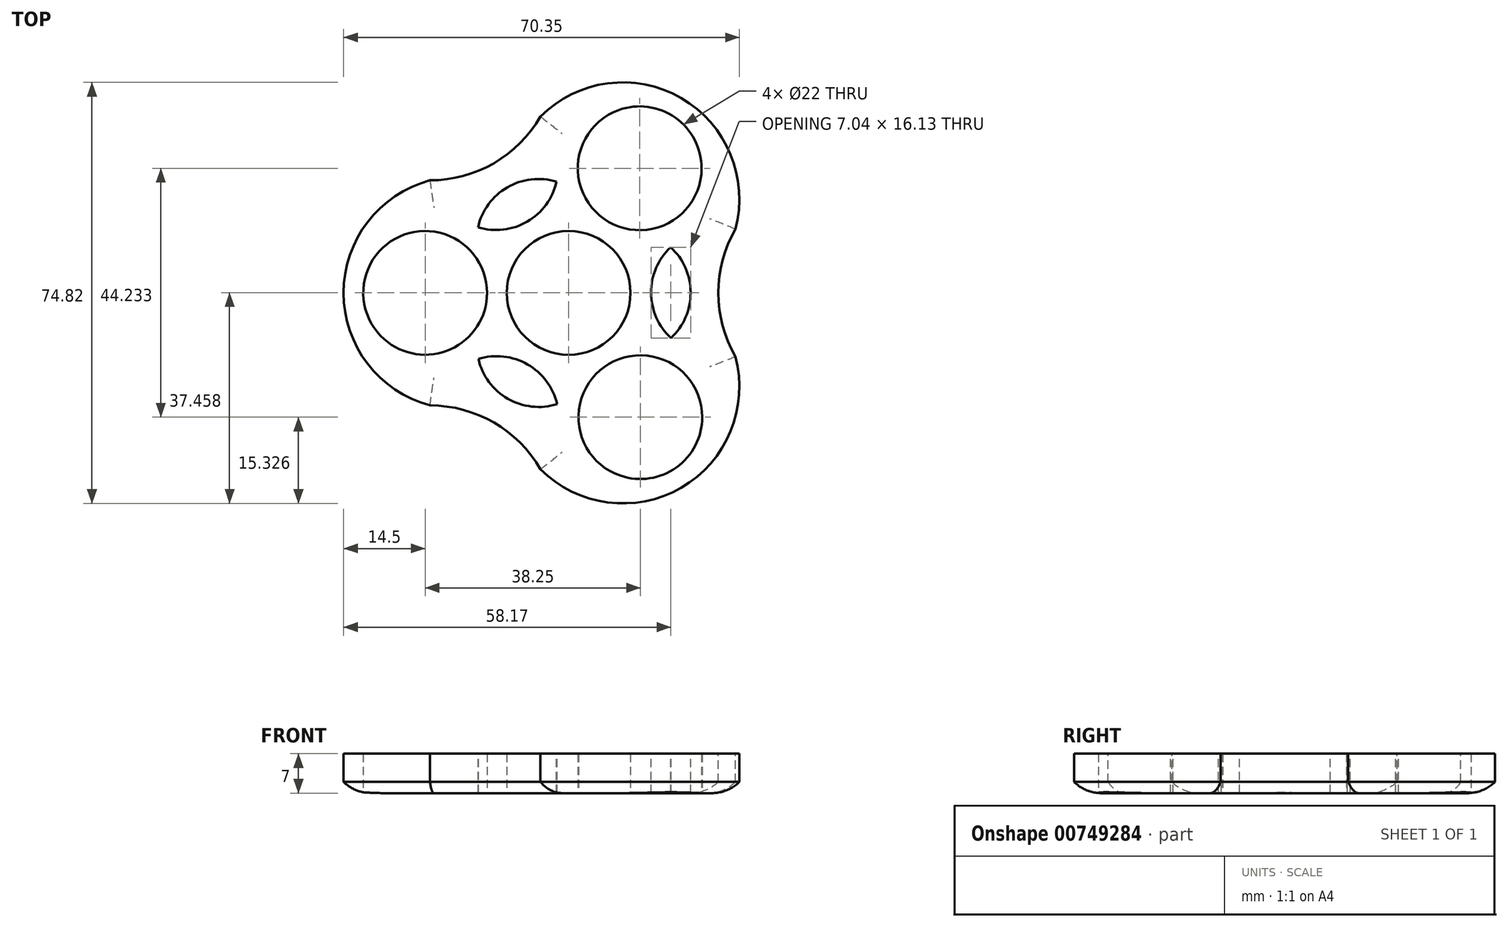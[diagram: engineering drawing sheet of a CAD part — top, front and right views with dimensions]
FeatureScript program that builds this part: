
annotation { "Feature Type Name" : "Feature", "Feature Type Description" : "" }
export const myFeature = defineFeature(function(context is Context, id is Id, definition is map)
    precondition{}
    {
        {
            var Q0;
            Q0=qCreatedBy(makeId("Top.planeOp"),FACE);
            var sketch = newSketch(context, id + "F0", { "sketchPlane" : qUnion([Q0])});
            skCircle(sketch, "E0", {"center": v(0, 0) * mm, "radius": 40 * mm});
            skCircle(sketch, "E1", {"center": v(0, 0) * mm, "radius": 11 * mm});
            skLineSegment(sketch, "E2", {"start": v(-11, 0) * mm, "end": v(-14.5, 0) * mm});
            skLineSegment(sketch, "E3", {"start": v(-14.5, 0) * mm, "end": v(-25.5, 0) * mm});
            skCircle(sketch, "E4", {"center": v(-25.5, 0) * mm, "radius": 11 * mm});
            skLineSegment(sketch, "E5", {"start": v(0, 0) * mm, "end": v(0, -40) * mm});
            skLineSegment(sketch, "E6", {"start": v(0, 0) * mm, "end": v(7.25, -12.56) * mm});
            skLineSegment(sketch, "E7", {"start": v(7.25, -12.56) * mm, "end": v(12.75, -22.08) * mm});
            skCircle(sketch, "E8", {"center": v(12.75, -22.08) * mm, "radius": 11 * mm});
            skLineSegment(sketch, "E9", {"start": v(0, 0) * mm, "end": v(0, 40) * mm});
            skLineSegment(sketch, "E10", {"start": v(0, 0) * mm, "end": v(7.25, 12.56) * mm});
            skLineSegment(sketch, "E11", {"start": v(7.25, 12.56) * mm, "end": v(12.63, 22.15) * mm});
            skCircle(sketch, "E12", {"center": v(12.63, 22.15) * mm, "radius": 11 * mm});
            skSolve(sketch);
        }
        {
            var Q0;
            Q0=makeQuery(id+"F0.imprint","IMPRINT",FACE,{"disambiguationData":[TD([[makeQuery(id+"F0.imprint","IMPRINT",EDGE,{"derivedFrom":sQuery(id+"F0.wireOp",EDGE,"E4")}),-1.0]])]});
            var Q1;
            Q1=makeQuery(id+"F0.imprint","IMPRINT",FACE,{"disambiguationData":[TD([[makeQuery(id+"F0.imprint","IMPRINT",EDGE,{"derivedFrom":sQuery(id+"F0.wireOp",EDGE,"E8")}),-1.0]])]});
            extrude(context, id + "F1", {"entities" : qUnion([Q0, Q1]), "depth" : 7 * mm, "offsetDistance" : 25 * mm});
        }
        {
            var Q0;
            Q0=makeQuery(id+"F1.opExtrude","CAP_FACE",FACE,{"disambiguationData":[OSD([sQuery(id+"F0.wireOp",EDGE,"E0"),sQuery(id+"F0.wireOp",EDGE,"E1"),sQuery(id+"F0.wireOp",EDGE,"E4"),sQuery(id+"F0.wireOp",EDGE,"E8"),sQuery(id+"F0.wireOp",EDGE,"E12")])],"isStart":false});
            var sketch = newSketch(context, id + "F2", { "sketchPlane" : qUnion([Q0])});
            skLineSegment(sketch, "E13", {"start": v(0, 0) * mm, "end": v(-40, 0) * mm});
            skLineSegment(sketch, "E14", {"start": v(0, 0) * mm, "end": v(25.32, -43.86) * mm});
            skLineSegment(sketch, "E15", {"start": v(0, 0) * mm, "end": v(28.72, 49.74) * mm});
            skLineSegment(sketch, "E16", {"start": v(-40, 0) * mm, "end": v(-40, 20) * mm});
            skLineSegment(sketch, "E17", {"start": v(-40, 0) * mm, "end": v(-40, -20) * mm});
            skLineSegment(sketch, "E18", {"start": v(-40, 20) * mm, "end": v(-34.64, 20) * mm});
            skLineSegment(sketch, "E19", {"start": v(-40, -20) * mm, "end": v(-34.64, -20) * mm});
            skLineSegment(sketch, "E20", {"start": v(25.32, -43.86) * mm, "end": v(20, -34.64) * mm});
            skLineSegment(sketch, "E21", {"start": v(20, -34.64) * mm, "end": v(2.68, -44.64) * mm});
            skLineSegment(sketch, "E22", {"start": v(20, -34.64) * mm, "end": v(37.32, -24.64) * mm});
            skLineSegment(sketch, "E23", {"start": v(28.72, 49.74) * mm, "end": v(20, 34.64) * mm});
            skLineSegment(sketch, "E24", {"start": v(20, 34.64) * mm, "end": v(37.32, 24.64) * mm});
            skLineSegment(sketch, "E25", {"start": v(20, 34.64) * mm, "end": v(2.68, 44.64) * mm});
            skLineSegment(sketch, "E26", {"start": v(2.68, 44.64) * mm, "end": v(0, 40) * mm});
            skLineSegment(sketch, "E27", {"start": v(37.32, 24.64) * mm, "end": v(34.64, 20) * mm});
            skLineSegment(sketch, "E28", {"start": v(2.68, -44.64) * mm, "end": v(0, -40) * mm});
            skLineSegment(sketch, "E29", {"start": v(37.32, -24.64) * mm, "end": v(34.64, -20) * mm});
            skLineSegment(sketch, "E30", {"start": v(34.64, 20) * mm, "end": v(29.64, 11.34) * mm});
            skArc(sketch, "E31", {"start": v(29.64, 11.34) * mm, "mid": v(28.78, 24.63) * mm, "end": v(20, 34.64) * mm});
            skLineSegment(sketch, "E32", {"start": v(34.64, -20) * mm, "end": v(29.64, -11.34) * mm});
            skArc(sketch, "E33", {"start": v(20, -34.64) * mm, "mid": v(28.78, -24.63) * mm, "end": v(29.64, -11.34) * mm});
            skArc(sketch, "E34", {"start": v(29.64, 11.34) * mm, "mid": v(26.6, 0) * mm, "end": v(29.64, -11.34) * mm});
            skLineSegment(sketch, "E35", {"start": v(0, 40) * mm, "end": v(-5, 31.34) * mm});
            skLineSegment(sketch, "E36", {"start": v(-34.64, 20) * mm, "end": v(-24.64, 20) * mm});
            skArc(sketch, "E37", {"start": v(-24.64, 20) * mm, "mid": v(-35.72, 12.6) * mm, "end": v(-40, 0) * mm});
            skArc(sketch, "E38", {"start": v(20, 34.64) * mm, "mid": v(6.94, 37.24) * mm, "end": v(-5, 31.34) * mm});
            skArc(sketch, "E39", {"start": v(-24.64, 20) * mm, "mid": v(-13.3, 23.04) * mm, "end": v(-5, 31.34) * mm});
            skLineSegment(sketch, "E40", {"start": v(-34.64, -20) * mm, "end": v(-24.64, -20) * mm});
            skLineSegment(sketch, "E41", {"start": v(0, -40) * mm, "end": v(-5, -31.34) * mm});
            skArc(sketch, "E42", {"start": v(-40, 0) * mm, "mid": v(-35.72, -12.6) * mm, "end": v(-24.64, -20) * mm});
            skArc(sketch, "E43", {"start": v(-5, -31.34) * mm, "mid": v(6.94, -37.24) * mm, "end": v(20, -34.64) * mm});
            skArc(sketch, "E44", {"start": v(-5, -31.34) * mm, "mid": v(-13.3, -23.04) * mm, "end": v(-24.64, -20) * mm});
            skSolve(sketch);
        }
        {
            var Q0;
            {var subQ0=sQuery(id+"F2.wireOp",EDGE,"E35");Q0=makeQuery(id+"F2.imprint","IMPRINT",FACE,{"disambiguationData":[TD([[makeQuery(id+"F2.imprint","IMPRINT",EDGE,{"derivedFrom":subQ0}),-1.0]])]});}
            var Q1;
            {var subQ0=sQuery(id+"F2.wireOp",EDGE,"E35");Q1=makeQuery(id+"F2.imprint","IMPRINT",FACE,{"disambiguationData":[TD([[makeQuery(id+"F2.imprint","IMPRINT",EDGE,{"derivedFrom":subQ0}),1.0]])]});}
            var Q2;
            {var subQ0=sQuery(id+"F2.wireOp",EDGE,"E36");Q2=makeQuery(id+"F2.imprint","IMPRINT",FACE,{"disambiguationData":[TD([[makeQuery(id+"F2.imprint","IMPRINT",EDGE,{"derivedFrom":subQ0}),-1.0]])]});}
            var Q3;
            {var subQ0=sQuery(id+"F2.wireOp",EDGE,"E40");Q3=makeQuery(id+"F2.imprint","IMPRINT",FACE,{"disambiguationData":[TD([[makeQuery(id+"F2.imprint","IMPRINT",EDGE,{"derivedFrom":subQ0}),1.0]])]});}
            var Q4;
            {var subQ0=sQuery(id+"F2.wireOp",EDGE,"E40");Q4=makeQuery(id+"F2.imprint","IMPRINT",FACE,{"disambiguationData":[TD([[makeQuery(id+"F2.imprint","IMPRINT",EDGE,{"derivedFrom":subQ0}),-1.0]])]});}
            var Q5;
            {var subQ0=sQuery(id+"F2.wireOp",EDGE,"E41");Q5=makeQuery(id+"F2.imprint","IMPRINT",FACE,{"disambiguationData":[TD([[makeQuery(id+"F2.imprint","IMPRINT",EDGE,{"derivedFrom":subQ0}),-1.0]])]});}
            var Q6;
            {var subQ0=sQuery(id+"F2.wireOp",EDGE,"E32");Q6=makeQuery(id+"F2.imprint","IMPRINT",FACE,{"disambiguationData":[TD([[makeQuery(id+"F2.imprint","IMPRINT",EDGE,{"derivedFrom":subQ0}),1.0]])]});}
            var Q7;
            {var subQ0=sQuery(id+"F2.wireOp",EDGE,"E30");Q7=makeQuery(id+"F2.imprint","IMPRINT",FACE,{"disambiguationData":[TD([[makeQuery(id+"F2.imprint","IMPRINT",EDGE,{"derivedFrom":subQ0}),1.0]])]});}
            var Q8;
            {var subQ0=sQuery(id+"F2.wireOp",EDGE,"E30");Q8=makeQuery(id+"F2.imprint","IMPRINT",FACE,{"disambiguationData":[TD([[makeQuery(id+"F2.imprint","IMPRINT",EDGE,{"derivedFrom":subQ0}),-1.0]])]});}
            extrude(context, id + "F3", {"entities" : qUnion([Q0, Q1, Q2, Q3, Q4, Q5, Q6, Q7, Q8]), "operationType" : NewBodyOperationType.REMOVE, "oppositeDirection" : true, "depth" : 25 * mm, "offsetDistance" : 25 * mm});
        }
        {
            var Q0;
            Q0=makeQuery(id+"F1.opExtrude","CAP_FACE",FACE,{"disambiguationData":[OSD([sQuery(id+"F0.wireOp",EDGE,"E0"),sQuery(id+"F0.wireOp",EDGE,"E1"),sQuery(id+"F0.wireOp",EDGE,"E4"),sQuery(id+"F0.wireOp",EDGE,"E8"),sQuery(id+"F0.wireOp",EDGE,"E12")])],"isStart":false});
            var sketch = newSketch(context, id + "F4", { "sketchPlane" : qUnion([Q0])});
            skArc(sketch, "E45", {"start": v(12.63, 22.15) * mm, "mid": v(-9.4, 16.2) * mm, "end": v(-25.5, 0) * mm});
            skLineSegment(sketch, "E46", {"start": v(-18.89, 8.8) * mm, "end": v(-16.1, 11.66) * mm});
            skLineSegment(sketch, "E47", {"start": v(1.72, 20.76) * mm, "end": v(-2.15, 19.76) * mm});
            skArc(sketch, "E48", {"start": v(-2.15, 19.76) * mm, "mid": v(-10.9, 18.76) * mm, "end": v(-16.1, 11.66) * mm});
            skArc(sketch, "E49", {"start": v(-16.1, 11.66) * mm, "mid": v(-7.36, 12.67) * mm, "end": v(-2.15, 19.76) * mm});
            skSolve(sketch);
        }
        {
            var Q0;
            {var subQ4=sQuery(id+"F4.wireOp",EDGE,"E48");Q0=makeQuery(id+"F4.imprint","IMPRINT",FACE,{"disambiguationData":[TD([[makeQuery(id+"F4.imprint","IMPRINT",EDGE,{"derivedFrom":subQ4}),1.0]])]});}
            var Q1;
            {var subQ0=sQuery(id+"F4.wireOp",EDGE,"E49");var subQ1=sQuery(id+"F4.wireOp",EDGE,"E45");var subQ2=makeQuery(id+"F4.imprint","INTERSECT",VERTEX,{"disambiguationData":[OD(0.0)],"derivedFrom":[subQ1,subQ0]});Q1=makeQuery(id+"F4.imprint","IMPRINT",FACE,{"disambiguationData":[TD([[makeQuery(id+"F4.imprint","IMPRINT",EDGE,{"disambiguationData":[TD([[subQ2,-1.0]])],"derivedFrom":subQ1}),1.0]])]});}
            extrude(context, id + "F5", {"entities" : qUnion([Q0, Q1]), "operationType" : NewBodyOperationType.REMOVE, "oppositeDirection" : true, "depth" : 25 * mm, "offsetDistance" : 25 * mm});
        }
        {
            var Q0;
            {var subQ4=sQuery(id+"F4.wireOp",EDGE,"E48");Q0=makeQuery(id+"F4.imprint","IMPRINT",FACE,{"disambiguationData":[TD([[makeQuery(id+"F4.imprint","IMPRINT",EDGE,{"derivedFrom":subQ4}),1.0]])]});}
            var Q1;
            {var subQ0=sQuery(id+"F4.wireOp",EDGE,"E49");var subQ1=sQuery(id+"F4.wireOp",EDGE,"E45");var subQ2=makeQuery(id+"F4.imprint","INTERSECT",VERTEX,{"disambiguationData":[OD(0.0)],"derivedFrom":[subQ1,subQ0]});Q1=makeQuery(id+"F4.imprint","IMPRINT",FACE,{"disambiguationData":[TD([[makeQuery(id+"F4.imprint","IMPRINT",EDGE,{"disambiguationData":[TD([[subQ2,-1.0]])],"derivedFrom":subQ1}),1.0]])]});}
            extrude(context, id + "F6", {"entities" : qUnion([Q0, Q1]), "operationType" : NewBodyOperationType.ADD, "depth" : 25 * mm, "offsetDistance" : 25 * mm});
        }
        {
            var Q0;
            Q0=makeQuery(id+"F6.opExtrude","SWEPT_BODY",BODY,{"disambiguationData":[OSD([sQuery(id+"F4.wireOp",EDGE,"E48"),sQuery(id+"F4.wireOp",EDGE,"E49")])]});
            var Q1;
            Q1=makeQuery(id+"F1.opExtrude","CAP_EDGE",EDGE,{"disambiguationData":[OSD([sQuery(id+"F0.wireOp",EDGE,"E1")])],"isStart":false});
            circularPattern(context, id + "F7", {"entities" : qUnion([Q0]), "axis" : qUnion([Q1]), "angle" : 360 * degree, "instanceCount" : 3, "equalSpace" : true});
        }
        {
            var Q0;
            Q0=makeQuery(id+"F7.opPattern","COPY",FACE,{"derivedFrom":makeQuery(id+"F6.opExtrude","CAP_FACE",FACE,{"disambiguationData":[OSD([sQuery(id+"F4.wireOp",EDGE,"E48"),sQuery(id+"F4.wireOp",EDGE,"E49")])],"isStart":false}),"instanceName":"2"});
            extrude(context, id + "F8", {"entities" : qUnion([Q0]), "operationType" : NewBodyOperationType.REMOVE, "endBound" : BoundingType.THROUGH_ALL, "oppositeDirection" : true, "depth" : 1000 * mm, "offsetDistance" : 25 * mm});
        }
        {
            var Q0;
            Q0=makeQuery(id+"F7.opPattern","COPY",FACE,{"derivedFrom":makeQuery(id+"F6.opExtrude","CAP_FACE",FACE,{"disambiguationData":[OSD([sQuery(id+"F4.wireOp",EDGE,"E48"),sQuery(id+"F4.wireOp",EDGE,"E49")])],"isStart":false}),"instanceName":"1"});
            var Q1;
            Q1=makeQuery(id+"F6.opExtrude","CAP_FACE",FACE,{"disambiguationData":[OSD([sQuery(id+"F4.wireOp",EDGE,"E48"),sQuery(id+"F4.wireOp",EDGE,"E49")])],"isStart":false});
            extrude(context, id + "F9", {"entities" : qUnion([Q0, Q1]), "operationType" : NewBodyOperationType.REMOVE, "endBound" : BoundingType.THROUGH_ALL, "oppositeDirection" : true, "depth" : 25 * mm, "offsetDistance" : 25 * mm});
        }
        {
            var Q0;
            Q0=makeQuery(id+"F3.boolean.opBoolean","COPY",EDGE,{"derivedFrom":makeQuery(id+"F3.opExtrude","CAP_EDGE",EDGE,{"disambiguationData":[OSD([sQuery(id+"F2.wireOp",EDGE,"E39")])],"isStart":true})});
            var Q1;
            Q1=makeQuery(id+"F3.boolean.opBoolean","TWEAK_EDGE",EDGE,{"derivedFrom":[makeQuery(id+"F3.opExtrude","CAP_EDGE",EDGE,{"disambiguationData":[OSD([sQuery(id+"F2.wireOp",EDGE,"E37")])],"isStart":true}),makeQuery(id+"F3.opExtrude","CAP_EDGE",EDGE,{"disambiguationData":[OSD([sQuery(id+"F2.wireOp",EDGE,"E42")])],"isStart":true})]});
            var Q2;
            Q2=makeQuery(id+"F3.boolean.opBoolean","TWEAK_EDGE",EDGE,{"derivedFrom":[makeQuery(id+"F3.opExtrude","CAP_EDGE",EDGE,{"disambiguationData":[OSD([sQuery(id+"F2.wireOp",EDGE,"E31")])],"isStart":true}),makeQuery(id+"F3.opExtrude","CAP_EDGE",EDGE,{"disambiguationData":[OSD([sQuery(id+"F2.wireOp",EDGE,"E38")])],"isStart":true})]});
            var Q3;
            Q3=makeQuery(id+"F3.boolean.opBoolean","COPY",EDGE,{"derivedFrom":makeQuery(id+"F3.opExtrude","CAP_EDGE",EDGE,{"disambiguationData":[OSD([sQuery(id+"F2.wireOp",EDGE,"E34")])],"isStart":true})});
            var Q4;
            Q4=makeQuery(id+"F3.boolean.opBoolean","TWEAK_EDGE",EDGE,{"derivedFrom":[makeQuery(id+"F3.opExtrude","CAP_EDGE",EDGE,{"disambiguationData":[OSD([sQuery(id+"F2.wireOp",EDGE,"E33")])],"isStart":true}),makeQuery(id+"F3.opExtrude","CAP_EDGE",EDGE,{"disambiguationData":[OSD([sQuery(id+"F2.wireOp",EDGE,"E43")])],"isStart":true})]});
            var Q5;
            Q5=makeQuery(id+"F3.boolean.opBoolean","COPY",EDGE,{"derivedFrom":makeQuery(id+"F3.opExtrude","CAP_EDGE",EDGE,{"disambiguationData":[OSD([sQuery(id+"F2.wireOp",EDGE,"E44")])],"isStart":true})});
            var Q6;
            Q6=makeQuery(id+"F3.boolean.opBoolean","INTERSECT",EDGE,{"derivedFrom":[makeQuery(id+"F1.opExtrude","CAP_FACE",FACE,{"disambiguationData":[OSD([sQuery(id+"F0.wireOp",EDGE,"E0"),sQuery(id+"F0.wireOp",EDGE,"E1"),sQuery(id+"F0.wireOp",EDGE,"E4"),sQuery(id+"F0.wireOp",EDGE,"E8"),sQuery(id+"F0.wireOp",EDGE,"E12")])],"isStart":true}),makeQuery(id+"F3.opExtrude","SWEPT_FACE",FACE,{"disambiguationData":[OSD([sQuery(id+"F2.wireOp",EDGE,"E37")])]}),makeQuery(id+"F3.opExtrude","SWEPT_FACE",FACE,{"disambiguationData":[OSD([sQuery(id+"F2.wireOp",EDGE,"E42")])]})]});
            var Q7;
            Q7=makeQuery(id+"F3.boolean.opBoolean","INTERSECT",EDGE,{"derivedFrom":[makeQuery(id+"F1.opExtrude","CAP_FACE",FACE,{"disambiguationData":[OSD([sQuery(id+"F0.wireOp",EDGE,"E0"),sQuery(id+"F0.wireOp",EDGE,"E1"),sQuery(id+"F0.wireOp",EDGE,"E4"),sQuery(id+"F0.wireOp",EDGE,"E8"),sQuery(id+"F0.wireOp",EDGE,"E12")])],"isStart":true}),makeQuery(id+"F3.opExtrude","SWEPT_FACE",FACE,{"disambiguationData":[OSD([sQuery(id+"F2.wireOp",EDGE,"E39")])]})]});
            var Q8;
            Q8=makeQuery(id+"F3.boolean.opBoolean","INTERSECT",EDGE,{"derivedFrom":[makeQuery(id+"F1.opExtrude","CAP_FACE",FACE,{"disambiguationData":[OSD([sQuery(id+"F0.wireOp",EDGE,"E0"),sQuery(id+"F0.wireOp",EDGE,"E1"),sQuery(id+"F0.wireOp",EDGE,"E4"),sQuery(id+"F0.wireOp",EDGE,"E8"),sQuery(id+"F0.wireOp",EDGE,"E12")])],"isStart":true}),makeQuery(id+"F3.opExtrude","SWEPT_FACE",FACE,{"disambiguationData":[OSD([sQuery(id+"F2.wireOp",EDGE,"E31")])]}),makeQuery(id+"F3.opExtrude","SWEPT_FACE",FACE,{"disambiguationData":[OSD([sQuery(id+"F2.wireOp",EDGE,"E38")])]})]});
            var Q9;
            Q9=makeQuery(id+"F3.boolean.opBoolean","INTERSECT",EDGE,{"derivedFrom":[makeQuery(id+"F1.opExtrude","CAP_FACE",FACE,{"disambiguationData":[OSD([sQuery(id+"F0.wireOp",EDGE,"E0"),sQuery(id+"F0.wireOp",EDGE,"E1"),sQuery(id+"F0.wireOp",EDGE,"E4"),sQuery(id+"F0.wireOp",EDGE,"E8"),sQuery(id+"F0.wireOp",EDGE,"E12")])],"isStart":true}),makeQuery(id+"F3.opExtrude","SWEPT_FACE",FACE,{"disambiguationData":[OSD([sQuery(id+"F2.wireOp",EDGE,"E34")])]})]});
            var Q10;
            Q10=makeQuery(id+"F3.boolean.opBoolean","INTERSECT",EDGE,{"derivedFrom":[makeQuery(id+"F1.opExtrude","CAP_FACE",FACE,{"disambiguationData":[OSD([sQuery(id+"F0.wireOp",EDGE,"E0"),sQuery(id+"F0.wireOp",EDGE,"E1"),sQuery(id+"F0.wireOp",EDGE,"E4"),sQuery(id+"F0.wireOp",EDGE,"E8"),sQuery(id+"F0.wireOp",EDGE,"E12")])],"isStart":true}),makeQuery(id+"F3.opExtrude","SWEPT_FACE",FACE,{"disambiguationData":[OSD([sQuery(id+"F2.wireOp",EDGE,"E33")])]}),makeQuery(id+"F3.opExtrude","SWEPT_FACE",FACE,{"disambiguationData":[OSD([sQuery(id+"F2.wireOp",EDGE,"E43")])]})]});
            var Q11;
            Q11=makeQuery(id+"F3.boolean.opBoolean","INTERSECT",EDGE,{"derivedFrom":[makeQuery(id+"F1.opExtrude","CAP_FACE",FACE,{"disambiguationData":[OSD([sQuery(id+"F0.wireOp",EDGE,"E0"),sQuery(id+"F0.wireOp",EDGE,"E1"),sQuery(id+"F0.wireOp",EDGE,"E4"),sQuery(id+"F0.wireOp",EDGE,"E8"),sQuery(id+"F0.wireOp",EDGE,"E12")])],"isStart":true}),makeQuery(id+"F3.opExtrude","SWEPT_FACE",FACE,{"disambiguationData":[OSD([sQuery(id+"F2.wireOp",EDGE,"E44")])]})]});
            chamfer(context, id + "F10", {"entities" : qUnion([Q0, Q1, Q2, Q3, Q4, Q5, Q6, Q7, Q8, Q9, Q10, Q11]), "width" : 2 * mm, "tangentPropagation" : true});
        }
        {
            var Q0;
            {var subQ0=makeQuery(id+"F1.opExtrude","CAP_FACE",FACE,{"disambiguationData":[OSD([sQuery(id+"F0.wireOp",EDGE,"E0"),sQuery(id+"F0.wireOp",EDGE,"E1"),sQuery(id+"F0.wireOp",EDGE,"E4"),sQuery(id+"F0.wireOp",EDGE,"E8"),sQuery(id+"F0.wireOp",EDGE,"E12")])],"isStart":true});Q0=makeQuery(id+"F10.opChamfer","BLEND_EDGE",EDGE,{"blendedFrom":[makeQuery(id+"F3.boolean.opBoolean","INTERSECT",EDGE,{"derivedFrom":[subQ0,makeQuery(id+"F3.opExtrude","SWEPT_FACE",FACE,{"disambiguationData":[OSD([sQuery(id+"F2.wireOp",EDGE,"E39")])]})]}),subQ0],"blendedInto":[subQ0]});}
            var Q1;
            {var subQ0=makeQuery(id+"F1.opExtrude","CAP_FACE",FACE,{"disambiguationData":[OSD([sQuery(id+"F0.wireOp",EDGE,"E0"),sQuery(id+"F0.wireOp",EDGE,"E1"),sQuery(id+"F0.wireOp",EDGE,"E4"),sQuery(id+"F0.wireOp",EDGE,"E8"),sQuery(id+"F0.wireOp",EDGE,"E12")])],"isStart":true});Q1=makeQuery(id+"F10.opChamfer","BLEND_EDGE",EDGE,{"blendedFrom":[makeQuery(id+"F3.boolean.opBoolean","INTERSECT",EDGE,{"derivedFrom":[subQ0,makeQuery(id+"F3.opExtrude","SWEPT_FACE",FACE,{"disambiguationData":[OSD([sQuery(id+"F2.wireOp",EDGE,"E37")])]}),makeQuery(id+"F3.opExtrude","SWEPT_FACE",FACE,{"disambiguationData":[OSD([sQuery(id+"F2.wireOp",EDGE,"E42")])]})]}),subQ0],"blendedInto":[subQ0]});}
            var Q2;
            {var subQ0=makeQuery(id+"F1.opExtrude","CAP_FACE",FACE,{"disambiguationData":[OSD([sQuery(id+"F0.wireOp",EDGE,"E0"),sQuery(id+"F0.wireOp",EDGE,"E1"),sQuery(id+"F0.wireOp",EDGE,"E4"),sQuery(id+"F0.wireOp",EDGE,"E8"),sQuery(id+"F0.wireOp",EDGE,"E12")])],"isStart":true});Q2=makeQuery(id+"F10.opChamfer","BLEND_EDGE",EDGE,{"blendedFrom":[makeQuery(id+"F3.boolean.opBoolean","INTERSECT",EDGE,{"derivedFrom":[subQ0,makeQuery(id+"F3.opExtrude","SWEPT_FACE",FACE,{"disambiguationData":[OSD([sQuery(id+"F2.wireOp",EDGE,"E44")])]})]}),subQ0],"blendedInto":[subQ0]});}
            var Q3;
            {var subQ0=makeQuery(id+"F1.opExtrude","CAP_FACE",FACE,{"disambiguationData":[OSD([sQuery(id+"F0.wireOp",EDGE,"E0"),sQuery(id+"F0.wireOp",EDGE,"E1"),sQuery(id+"F0.wireOp",EDGE,"E4"),sQuery(id+"F0.wireOp",EDGE,"E8"),sQuery(id+"F0.wireOp",EDGE,"E12")])],"isStart":true});Q3=makeQuery(id+"F10.opChamfer","BLEND_EDGE",EDGE,{"blendedFrom":[makeQuery(id+"F3.boolean.opBoolean","INTERSECT",EDGE,{"derivedFrom":[subQ0,makeQuery(id+"F3.opExtrude","SWEPT_FACE",FACE,{"disambiguationData":[OSD([sQuery(id+"F2.wireOp",EDGE,"E33")])]}),makeQuery(id+"F3.opExtrude","SWEPT_FACE",FACE,{"disambiguationData":[OSD([sQuery(id+"F2.wireOp",EDGE,"E43")])]})]}),subQ0],"blendedInto":[subQ0]});}
            var Q4;
            {var subQ0=makeQuery(id+"F1.opExtrude","CAP_FACE",FACE,{"disambiguationData":[OSD([sQuery(id+"F0.wireOp",EDGE,"E0"),sQuery(id+"F0.wireOp",EDGE,"E1"),sQuery(id+"F0.wireOp",EDGE,"E4"),sQuery(id+"F0.wireOp",EDGE,"E8"),sQuery(id+"F0.wireOp",EDGE,"E12")])],"isStart":true});Q4=makeQuery(id+"F10.opChamfer","BLEND_EDGE",EDGE,{"blendedFrom":[makeQuery(id+"F3.boolean.opBoolean","INTERSECT",EDGE,{"derivedFrom":[subQ0,makeQuery(id+"F3.opExtrude","SWEPT_FACE",FACE,{"disambiguationData":[OSD([sQuery(id+"F2.wireOp",EDGE,"E34")])]})]}),subQ0],"blendedInto":[subQ0]});}
            var Q5;
            {var subQ0=makeQuery(id+"F1.opExtrude","CAP_FACE",FACE,{"disambiguationData":[OSD([sQuery(id+"F0.wireOp",EDGE,"E0"),sQuery(id+"F0.wireOp",EDGE,"E1"),sQuery(id+"F0.wireOp",EDGE,"E4"),sQuery(id+"F0.wireOp",EDGE,"E8"),sQuery(id+"F0.wireOp",EDGE,"E12")])],"isStart":true});Q5=makeQuery(id+"F10.opChamfer","BLEND_EDGE",EDGE,{"blendedFrom":[makeQuery(id+"F3.boolean.opBoolean","INTERSECT",EDGE,{"derivedFrom":[subQ0,makeQuery(id+"F3.opExtrude","SWEPT_FACE",FACE,{"disambiguationData":[OSD([sQuery(id+"F2.wireOp",EDGE,"E31")])]}),makeQuery(id+"F3.opExtrude","SWEPT_FACE",FACE,{"disambiguationData":[OSD([sQuery(id+"F2.wireOp",EDGE,"E38")])]})]}),subQ0],"blendedInto":[subQ0]});}
            var Q6;
            Q6=makeQuery(id+"F10.opChamfer","BLEND_EDGE",EDGE,{"blendedFrom":[makeQuery(id+"F3.boolean.opBoolean","TWEAK_EDGE",EDGE,{"derivedFrom":[makeQuery(id+"F3.opExtrude","CAP_EDGE",EDGE,{"disambiguationData":[OSD([sQuery(id+"F2.wireOp",EDGE,"E31")])],"isStart":true}),makeQuery(id+"F3.opExtrude","CAP_EDGE",EDGE,{"disambiguationData":[OSD([sQuery(id+"F2.wireOp",EDGE,"E38")])],"isStart":true})]}),makeQuery(id+"F1.opExtrude","CAP_FACE",FACE,{"disambiguationData":[OSD([sQuery(id+"F0.wireOp",EDGE,"E0"),sQuery(id+"F0.wireOp",EDGE,"E1"),sQuery(id+"F0.wireOp",EDGE,"E4"),sQuery(id+"F0.wireOp",EDGE,"E8"),sQuery(id+"F0.wireOp",EDGE,"E12")])],"isStart":false})],"blendedInto":[makeQuery(id+"F1.opExtrude","CAP_FACE",FACE,{"disambiguationData":[OSD([sQuery(id+"F0.wireOp",EDGE,"E0"),sQuery(id+"F0.wireOp",EDGE,"E1"),sQuery(id+"F0.wireOp",EDGE,"E4"),sQuery(id+"F0.wireOp",EDGE,"E8"),sQuery(id+"F0.wireOp",EDGE,"E12")])],"isStart":false})]});
            var Q7;
            Q7=makeQuery(id+"F10.opChamfer","BLEND_EDGE",EDGE,{"blendedFrom":[makeQuery(id+"F3.boolean.opBoolean","COPY",EDGE,{"derivedFrom":makeQuery(id+"F3.opExtrude","CAP_EDGE",EDGE,{"disambiguationData":[OSD([sQuery(id+"F2.wireOp",EDGE,"E34")])],"isStart":true})}),makeQuery(id+"F1.opExtrude","CAP_FACE",FACE,{"disambiguationData":[OSD([sQuery(id+"F0.wireOp",EDGE,"E0"),sQuery(id+"F0.wireOp",EDGE,"E1"),sQuery(id+"F0.wireOp",EDGE,"E4"),sQuery(id+"F0.wireOp",EDGE,"E8"),sQuery(id+"F0.wireOp",EDGE,"E12")])],"isStart":false})],"blendedInto":[makeQuery(id+"F1.opExtrude","CAP_FACE",FACE,{"disambiguationData":[OSD([sQuery(id+"F0.wireOp",EDGE,"E0"),sQuery(id+"F0.wireOp",EDGE,"E1"),sQuery(id+"F0.wireOp",EDGE,"E4"),sQuery(id+"F0.wireOp",EDGE,"E8"),sQuery(id+"F0.wireOp",EDGE,"E12")])],"isStart":false})]});
            var Q8;
            Q8=makeQuery(id+"F10.opChamfer","BLEND_EDGE",EDGE,{"blendedFrom":[makeQuery(id+"F3.boolean.opBoolean","TWEAK_EDGE",EDGE,{"derivedFrom":[makeQuery(id+"F3.opExtrude","CAP_EDGE",EDGE,{"disambiguationData":[OSD([sQuery(id+"F2.wireOp",EDGE,"E33")])],"isStart":true}),makeQuery(id+"F3.opExtrude","CAP_EDGE",EDGE,{"disambiguationData":[OSD([sQuery(id+"F2.wireOp",EDGE,"E43")])],"isStart":true})]}),makeQuery(id+"F1.opExtrude","CAP_FACE",FACE,{"disambiguationData":[OSD([sQuery(id+"F0.wireOp",EDGE,"E0"),sQuery(id+"F0.wireOp",EDGE,"E1"),sQuery(id+"F0.wireOp",EDGE,"E4"),sQuery(id+"F0.wireOp",EDGE,"E8"),sQuery(id+"F0.wireOp",EDGE,"E12")])],"isStart":false})],"blendedInto":[makeQuery(id+"F1.opExtrude","CAP_FACE",FACE,{"disambiguationData":[OSD([sQuery(id+"F0.wireOp",EDGE,"E0"),sQuery(id+"F0.wireOp",EDGE,"E1"),sQuery(id+"F0.wireOp",EDGE,"E4"),sQuery(id+"F0.wireOp",EDGE,"E8"),sQuery(id+"F0.wireOp",EDGE,"E12")])],"isStart":false})]});
            var Q9;
            Q9=makeQuery(id+"F10.opChamfer","BLEND_EDGE",EDGE,{"blendedFrom":[makeQuery(id+"F3.boolean.opBoolean","COPY",EDGE,{"derivedFrom":makeQuery(id+"F3.opExtrude","CAP_EDGE",EDGE,{"disambiguationData":[OSD([sQuery(id+"F2.wireOp",EDGE,"E44")])],"isStart":true})}),makeQuery(id+"F1.opExtrude","CAP_FACE",FACE,{"disambiguationData":[OSD([sQuery(id+"F0.wireOp",EDGE,"E0"),sQuery(id+"F0.wireOp",EDGE,"E1"),sQuery(id+"F0.wireOp",EDGE,"E4"),sQuery(id+"F0.wireOp",EDGE,"E8"),sQuery(id+"F0.wireOp",EDGE,"E12")])],"isStart":false})],"blendedInto":[makeQuery(id+"F1.opExtrude","CAP_FACE",FACE,{"disambiguationData":[OSD([sQuery(id+"F0.wireOp",EDGE,"E0"),sQuery(id+"F0.wireOp",EDGE,"E1"),sQuery(id+"F0.wireOp",EDGE,"E4"),sQuery(id+"F0.wireOp",EDGE,"E8"),sQuery(id+"F0.wireOp",EDGE,"E12")])],"isStart":false})]});
            var Q10;
            Q10=makeQuery(id+"F10.opChamfer","BLEND_EDGE",EDGE,{"blendedFrom":[makeQuery(id+"F3.boolean.opBoolean","TWEAK_EDGE",EDGE,{"derivedFrom":[makeQuery(id+"F3.opExtrude","CAP_EDGE",EDGE,{"disambiguationData":[OSD([sQuery(id+"F2.wireOp",EDGE,"E37")])],"isStart":true}),makeQuery(id+"F3.opExtrude","CAP_EDGE",EDGE,{"disambiguationData":[OSD([sQuery(id+"F2.wireOp",EDGE,"E42")])],"isStart":true})]}),makeQuery(id+"F1.opExtrude","CAP_FACE",FACE,{"disambiguationData":[OSD([sQuery(id+"F0.wireOp",EDGE,"E0"),sQuery(id+"F0.wireOp",EDGE,"E1"),sQuery(id+"F0.wireOp",EDGE,"E4"),sQuery(id+"F0.wireOp",EDGE,"E8"),sQuery(id+"F0.wireOp",EDGE,"E12")])],"isStart":false})],"blendedInto":[makeQuery(id+"F1.opExtrude","CAP_FACE",FACE,{"disambiguationData":[OSD([sQuery(id+"F0.wireOp",EDGE,"E0"),sQuery(id+"F0.wireOp",EDGE,"E1"),sQuery(id+"F0.wireOp",EDGE,"E4"),sQuery(id+"F0.wireOp",EDGE,"E8"),sQuery(id+"F0.wireOp",EDGE,"E12")])],"isStart":false})]});
            var Q11;
            Q11=makeQuery(id+"F10.opChamfer","BLEND_EDGE",EDGE,{"blendedFrom":[makeQuery(id+"F3.boolean.opBoolean","COPY",EDGE,{"derivedFrom":makeQuery(id+"F3.opExtrude","CAP_EDGE",EDGE,{"disambiguationData":[OSD([sQuery(id+"F2.wireOp",EDGE,"E39")])],"isStart":true})}),makeQuery(id+"F1.opExtrude","CAP_FACE",FACE,{"disambiguationData":[OSD([sQuery(id+"F0.wireOp",EDGE,"E0"),sQuery(id+"F0.wireOp",EDGE,"E1"),sQuery(id+"F0.wireOp",EDGE,"E4"),sQuery(id+"F0.wireOp",EDGE,"E8"),sQuery(id+"F0.wireOp",EDGE,"E12")])],"isStart":false})],"blendedInto":[makeQuery(id+"F1.opExtrude","CAP_FACE",FACE,{"disambiguationData":[OSD([sQuery(id+"F0.wireOp",EDGE,"E0"),sQuery(id+"F0.wireOp",EDGE,"E1"),sQuery(id+"F0.wireOp",EDGE,"E4"),sQuery(id+"F0.wireOp",EDGE,"E8"),sQuery(id+"F0.wireOp",EDGE,"E12")])],"isStart":false})]});
            fillet(context, id + "F11", {"entities" : qUnion([Q0, Q1, Q2, Q3, Q4, Q5, Q6, Q7, Q8, Q9, Q10, Q11]), "radius" : 7 * mm, "tangentPropagation" : true, "allowEdgeOverflow" : false});
        }
    });
